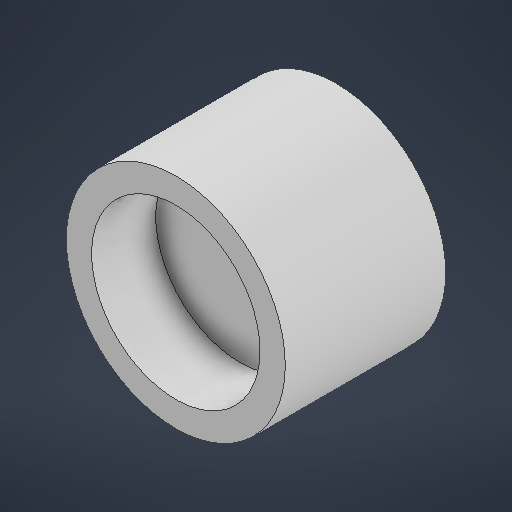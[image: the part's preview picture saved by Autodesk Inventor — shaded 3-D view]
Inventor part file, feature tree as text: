
AUTODESK INVENTOR PART (.ipt)
format: ipt  version: 2025.3 (Build 293356030, 356C)  size: 194,560 bytes
history: native  units: mm
features: extrude x3, sketch x2
ambient origin geometry x8: Origin, YZ Plane, XZ Plane, XY Plane, X Axis, Y Axis, Z Axis, Center Point
bodies: Solid1 (feature_tree)
feature tree (5):
  sketch  "Sketch1"  dims[d0=10.5mm d1=13.65mm]
  extrude  "Extrusion1"  Depth=13.65mm
  extrude  "Extrusion2"  Depth=6.0mm TaperAngle=0.0deg
  extrude  "Extrusion3"  Depth=4.0mm
  sketch  "Sketch2"  dims[d2=4.0mm d3=0.0mm d4=6.0mm d5=0.0mm d6=7.0mm d7=0.7mm d8=4.0mm d9=0.0mm]
